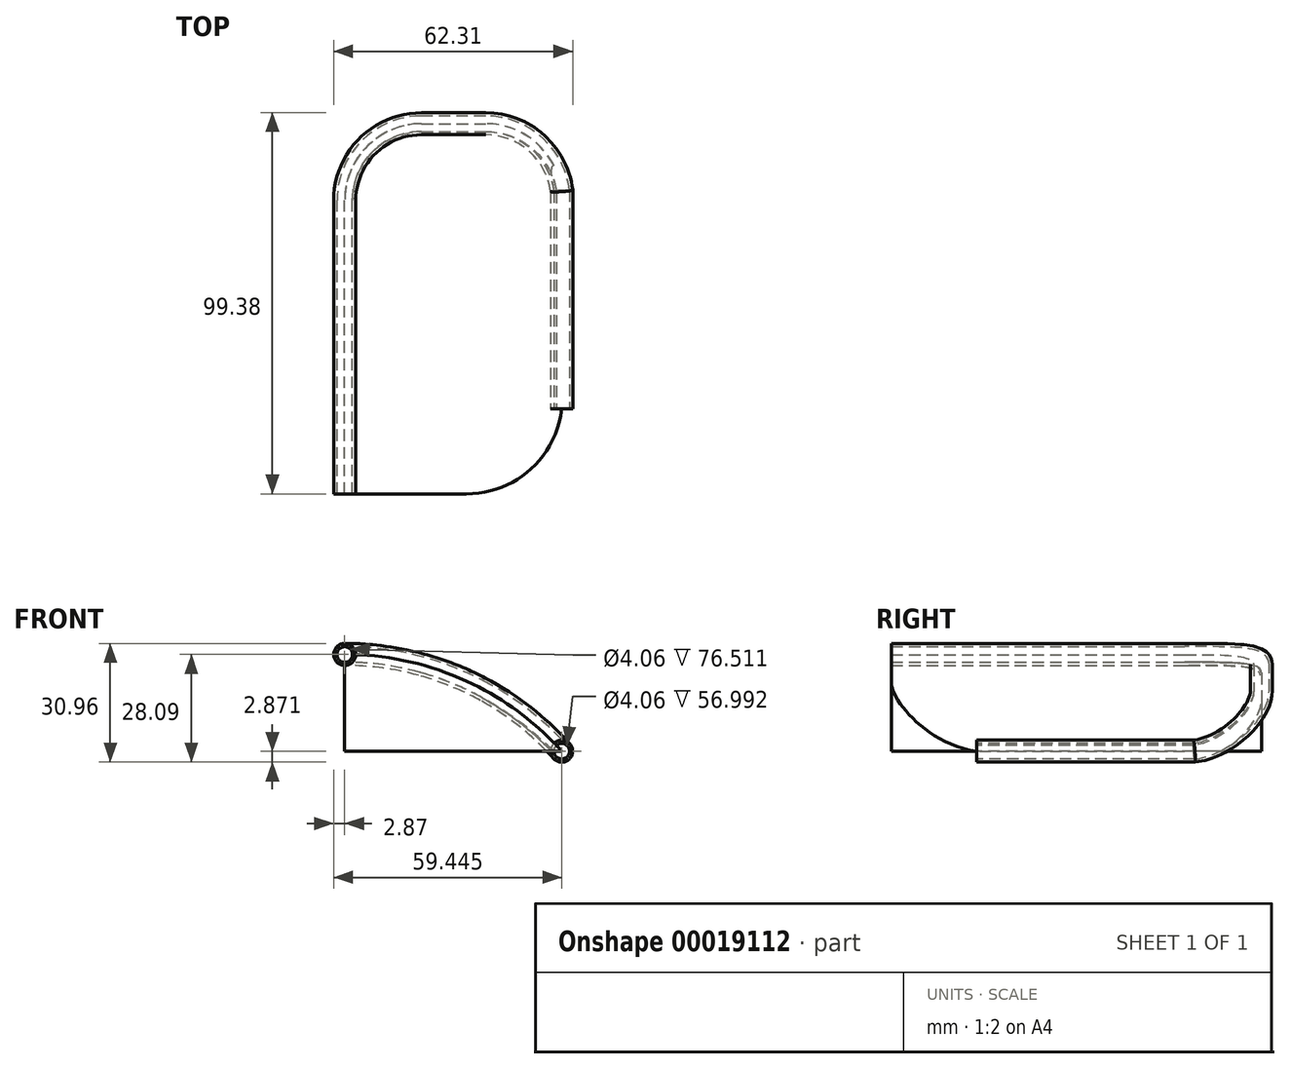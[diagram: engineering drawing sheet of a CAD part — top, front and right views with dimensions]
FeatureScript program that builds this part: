
annotation { "Feature Type Name" : "Feature", "Feature Type Description" : "" }
export const myFeature = defineFeature(function(context is Context, id is Id, definition is map)
    precondition{}
    {
        {
            var Q0;
            Q0=qCreatedBy(makeId("Front.planeOp"),FACE);
            var sketch = newSketch(context, id + "F0", { "sketchPlane" : qUnion([Q0])});
            skLineSegment(sketch, "E0.bottom", {"start": v(0, 0) * mm, "end": v(56.73, 0) * mm});
            skLineSegment(sketch, "E0.top", {"start": v(0, -44.24) * mm, "end": v(56.73, -44.24) * mm});
            skLineSegment(sketch, "E0.left", {"start": v(0, 0) * mm, "end": v(0, -44.24) * mm});
            skLineSegment(sketch, "E0.right", {"start": v(56.73, 0) * mm, "end": v(56.73, -44.24) * mm});
            skSolve(sketch);
        }
        {
            var Q0;
            Q0=makeQuery(id+"F0.imprint","IMPRINT",FACE,{"disambiguationData":[TD([[makeQuery(id+"F0.imprint","IMPRINT",EDGE,{"derivedFrom":sQuery(id+"F0.wireOp",EDGE,"E0.bottom")}),-1.0]])]});
            extrude(context, id + "F1", {"entities" : qUnion([Q0]), "depth" : 96.51 * mm});
        }
        {
            var Q0;
            Q0=makeQuery(id+"F1.opExtrude","CAP_FACE",FACE,{"disambiguationData":[OSD([sQuery(id+"F0.wireOp",EDGE,"E0.bottom"),sQuery(id+"F0.wireOp",EDGE,"E0.top"),sQuery(id+"F0.wireOp",EDGE,"E0.left"),sQuery(id+"F0.wireOp",EDGE,"E0.right")])],"isStart":false});
            var sketch = newSketch(context, id + "F2", { "sketchPlane" : qUnion([Q0])});
            skArc(sketch, "E1", {"start": v(56.73, -25.4) * mm, "mid": v(31.08, -6.64) * mm, "end": v(0, 0) * mm});
            skLineSegment(sketch, "E2", {"start": v(56.73, -25.4) * mm, "end": v(64.92, -10.77) * mm});
            skLineSegment(sketch, "E3", {"start": v(64.92, -10.77) * mm, "end": v(58.4, 12.94) * mm});
            skLineSegment(sketch, "E4", {"start": v(58.4, 12.94) * mm, "end": v(0, 7.8) * mm});
            skLineSegment(sketch, "E5", {"start": v(0, 7.8) * mm, "end": v(0, 0) * mm});
            skSolve(sketch);
        }
        {
            var Q0;
            {var subQ1=sQuery(id+"F2.wireOp",EDGE,"E1");Q0=makeQuery(id+"F2.imprint","IMPRINT",FACE,{"disambiguationData":[TD([[makeQuery(id+"F2.imprint","IMPRINT",EDGE,{"derivedFrom":subQ1}),-1.0]])]});}
            var Q1;
            {var subQ1=sQuery(id+"F2.wireOp",EDGE,"E2");Q1=makeQuery(id+"F2.imprint","IMPRINT",FACE,{"disambiguationData":[TD([[makeQuery(id+"F2.imprint","IMPRINT",EDGE,{"derivedFrom":subQ1}),1.0]])]});}
            extrude(context, id + "F3", {"entities" : qUnion([Q0, Q1]), "operationType" : NewBodyOperationType.REMOVE, "oppositeDirection" : true, "depth" : 104.35 * mm});
        }
        {
            var Q0;
            Q0=makeQuery(id+"F1.opExtrude","CAP_EDGE",EDGE,{"disambiguationData":[OSD([sQuery(id+"F0.wireOp",EDGE,"E0.right")])],"isStart":true});
            fillet(context, id + "F4", {"entities" : qUnion([Q0]), "radius" : 20 * mm, "tangentPropagation" : true, "allowEdgeOverflow" : false});
        }
        {
            var Q0;
            Q0=makeQuery(id+"F1.opExtrude","CAP_EDGE",EDGE,{"disambiguationData":[OSD([sQuery(id+"F0.wireOp",EDGE,"E0.left")])],"isStart":true});
            fillet(context, id + "F5", {"entities" : qUnion([Q0]), "radius" : 20 * mm, "tangentPropagation" : true, "allowEdgeOverflow" : false});
        }
        {
            var Q0;
            Q0=makeQuery(id+"F1.opExtrude","CAP_FACE",FACE,{"disambiguationData":[OSD([sQuery(id+"F0.wireOp",EDGE,"E0.bottom"),sQuery(id+"F0.wireOp",EDGE,"E0.top"),sQuery(id+"F0.wireOp",EDGE,"E0.left"),sQuery(id+"F0.wireOp",EDGE,"E0.right")])],"isStart":false});
            var sketch = newSketch(context, id + "F6", { "sketchPlane" : qUnion([Q0])});
            skCircle(sketch, "E6", {"center": v(0, 0) * mm, "radius": 2.87 * mm});
            skSolve(sketch);
        }
        {
            var Q0;
            Q0=makeQuery(id+"F1.opExtrude","CAP_EDGE",EDGE,{"disambiguationData":[OSD([sQuery(id+"F0.wireOp",EDGE,"E0.right")])],"isStart":false});
            fillet(context, id + "F7", {"entities" : qUnion([Q0]), "radius" : 25 * mm, "tangentPropagation" : true, "allowEdgeOverflow" : false});
        }
        {
            var Q0;
            Q0=makeQuery(id+"F1.opExtrude","SWEPT_FACE",FACE,{"disambiguationData":[OSD([sQuery(id+"F0.wireOp",EDGE,"E0.top")])]});
            extrude(context, id + "F8", {"entities" : qUnion([Q0]), "operationType" : NewBodyOperationType.REMOVE, "oppositeDirection" : true, "depth" : 19.02 * mm});
        }
        {
            var Q0;
            {var subQ1=sQuery(id+"F6.wireOp",EDGE,"E6");var subQ3=makeQuery(id+"F1.opExtrude","CAP_EDGE",EDGE,{"disambiguationData":[OSD([sQuery(id+"F0.wireOp",EDGE,"E0.left")])],"isStart":false});var subQ5=makeQuery(id+"F6.imprint","INTERSECT",VERTEX,{"derivedFrom":[subQ3,subQ1]});Q0=makeQuery(id+"F6.imprint","IMPRINT",FACE,{"disambiguationData":[TD([[makeQuery(id+"F6.imprint","IMPRINT",EDGE,{"disambiguationData":[TD([[subQ5,1.0]])],"derivedFrom":subQ1}),1.0]])]});}
            var Q1;
            {var subQ1=sQuery(id+"F6.wireOp",EDGE,"E6");var subQ3=makeQuery(id+"F1.opExtrude","CAP_EDGE",EDGE,{"disambiguationData":[OSD([sQuery(id+"F0.wireOp",EDGE,"E0.left")])],"isStart":false});var subQ5=makeQuery(id+"F6.imprint","INTERSECT",VERTEX,{"derivedFrom":[subQ3,subQ1]});Q1=makeQuery(id+"F6.imprint","IMPRINT",FACE,{"disambiguationData":[TD([[makeQuery(id+"F6.imprint","IMPRINT",EDGE,{"disambiguationData":[TD([[subQ5,-1.0]])],"derivedFrom":subQ1}),1.0]])]});}
            var Q2;
            {var subQ0=sQuery(id+"F0.wireOp",EDGE,"E0.bottom");var subQ1=sQuery(id+"F0.wireOp",EDGE,"E0.left");Q2=makeQuery(id+"F3.boolean.opBoolean","MERGE",EDGE,{"derivedFrom":[makeQuery(id+"F1.opExtrude","SWEPT_EDGE",EDGE,{"disambiguationData":[OSD([subQ0,subQ1])]}),makeQuery(id+"F3.opExtrude","SWEPT_EDGE",EDGE,{"disambiguationData":[OSD([subQ0,subQ1,sQuery(id+"F2.wireOp",EDGE,"E1"),sQuery(id+"F2.wireOp",EDGE,"E5")])]})]});}
            var Q3;
            Q3=makeQuery(id+"F5.opFillet","BLEND_EDGE",EDGE,{"blendedFrom":[makeQuery(id+"F1.opExtrude","CAP_EDGE",EDGE,{"disambiguationData":[OSD([sQuery(id+"F0.wireOp",EDGE,"E0.left")])],"isStart":true}),makeQuery(id+"F3.boolean.opBoolean","COPY",FACE,{"derivedFrom":makeQuery(id+"F3.opExtrude","SWEPT_FACE",FACE,{"disambiguationData":[OSD([sQuery(id+"F2.wireOp",EDGE,"E1")])]})})],"blendedInto":[makeQuery(id+"F3.boolean.opBoolean","COPY",FACE,{"derivedFrom":makeQuery(id+"F3.opExtrude","SWEPT_FACE",FACE,{"disambiguationData":[OSD([sQuery(id+"F2.wireOp",EDGE,"E1")])]})})]});
            var Q4;
            Q4=makeQuery(id+"F3.boolean.opBoolean","INTERSECT",EDGE,{"derivedFrom":[makeQuery(id+"F1.opExtrude","CAP_FACE",FACE,{"disambiguationData":[OSD([sQuery(id+"F0.wireOp",EDGE,"E0.bottom"),sQuery(id+"F0.wireOp",EDGE,"E0.top"),sQuery(id+"F0.wireOp",EDGE,"E0.left"),sQuery(id+"F0.wireOp",EDGE,"E0.right")])],"isStart":true}),makeQuery(id+"F3.opExtrude","SWEPT_FACE",FACE,{"disambiguationData":[OSD([sQuery(id+"F2.wireOp",EDGE,"E1")])]})]});
            var Q5;
            Q5=makeQuery(id+"F4.opFillet","BLEND_EDGE",EDGE,{"blendedFrom":[makeQuery(id+"F1.opExtrude","CAP_EDGE",EDGE,{"disambiguationData":[OSD([sQuery(id+"F0.wireOp",EDGE,"E0.right")])],"isStart":true}),makeQuery(id+"F3.boolean.opBoolean","COPY",FACE,{"derivedFrom":makeQuery(id+"F3.opExtrude","SWEPT_FACE",FACE,{"disambiguationData":[OSD([sQuery(id+"F2.wireOp",EDGE,"E1")])]})})],"blendedInto":[makeQuery(id+"F3.boolean.opBoolean","COPY",FACE,{"derivedFrom":makeQuery(id+"F3.opExtrude","SWEPT_FACE",FACE,{"disambiguationData":[OSD([sQuery(id+"F2.wireOp",EDGE,"E1")])]})})]});
            var Q6;
            Q6=makeQuery(id+"F8.boolean.opBoolean","INTERSECT",EDGE,{"derivedFrom":[makeQuery(id+"F3.boolean.opBoolean","COPY",FACE,{"derivedFrom":makeQuery(id+"F3.opExtrude","SWEPT_FACE",FACE,{"disambiguationData":[OSD([sQuery(id+"F2.wireOp",EDGE,"E1")])]})}),makeQuery(id+"F8.opExtrude","CAP_FACE",FACE,{"disambiguationData":[OSD([sQuery(id+"F0.wireOp",EDGE,"E0.top")])],"isStart":false})]});
            var Q7;
            {var subQ0=sQuery(id+"F0.wireOp",EDGE,"E0.top");var subQ1=sQuery(id+"F0.wireOp",EDGE,"E0.right");Q7=makeQuery(id+"F8.boolean.opBoolean","COPY",EDGE,{"derivedFrom":makeQuery(id+"F8.opExtrude","CAP_EDGE",EDGE,{"disambiguationData":[OSD([subQ0,subQ1]),TDD([makeQuery(id+"F7.opFillet","BLEND_EDGE",EDGE,{"blendedFrom":[makeQuery(id+"F1.opExtrude","CAP_EDGE",EDGE,{"disambiguationData":[OSD([subQ1])],"isStart":false}),makeQuery(id+"F1.opExtrude","SWEPT_FACE",FACE,{"disambiguationData":[OSD([subQ0])]})],"blendedInto":[makeQuery(id+"F1.opExtrude","SWEPT_FACE",FACE,{"disambiguationData":[OSD([subQ0])]})]})])],"isStart":false})});}
            var Q8;
            {var subQ0=sQuery(id+"F0.wireOp",EDGE,"E0.top");Q8=makeQuery(id+"F8.boolean.opBoolean","COPY",EDGE,{"derivedFrom":makeQuery(id+"F8.opExtrude","CAP_EDGE",EDGE,{"disambiguationData":[OSD([subQ0]),TDD([makeQuery(id+"F1.opExtrude","CAP_EDGE",EDGE,{"disambiguationData":[OSD([subQ0])],"isStart":false})])],"isStart":false})});}
            sweep(context, id + "F9", {"profiles" : qUnion([Q0, Q1]), "path" : qUnion([Q2, Q3, Q4, Q5, Q6, Q7, Q8])});
        }
        {
            var Q0;
            Q0=makeQuery(id+"F9.opSweep","CAP_FACE",FACE,{"disambiguationData":[OSD([sQuery(id+"F0.wireOp",EDGE,"E0.bottom"),sQuery(id+"F0.wireOp",EDGE,"E0.left"),sQuery(id+"F2.wireOp",EDGE,"E1"),sQuery(id+"F2.wireOp",EDGE,"E5"),sQuery(id+"F6.wireOp",EDGE,"E6")])],"isStart":true});
            var sketch = newSketch(context, id + "F10", { "sketchPlane" : qUnion([Q0])});
            skCircle(sketch, "E7", {"center": v(0, 0) * mm, "radius": 2.03 * mm});
            skSolve(sketch);
        }
        {
            var Q0;
            Q0=makeQuery(id+"F10.imprint","IMPRINT",FACE,{"disambiguationData":[TD([[makeQuery(id+"F10.imprint","IMPRINT",EDGE,{"derivedFrom":sQuery(id+"F10.wireOp",EDGE,"E7")}),1.0]])]});
            var Q1;
            {var subQ0=sQuery(id+"F0.wireOp",EDGE,"E0.bottom");var subQ1=sQuery(id+"F0.wireOp",EDGE,"E0.left");Q1=makeQuery(id+"F3.boolean.opBoolean","MERGE",EDGE,{"derivedFrom":[makeQuery(id+"F1.opExtrude","SWEPT_EDGE",EDGE,{"disambiguationData":[OSD([subQ0,subQ1])]}),makeQuery(id+"F3.opExtrude","SWEPT_EDGE",EDGE,{"disambiguationData":[OSD([subQ0,subQ1,sQuery(id+"F2.wireOp",EDGE,"E1"),sQuery(id+"F2.wireOp",EDGE,"E5")])]})]});}
            var Q2;
            Q2=makeQuery(id+"F5.opFillet","BLEND_EDGE",EDGE,{"blendedFrom":[makeQuery(id+"F1.opExtrude","CAP_EDGE",EDGE,{"disambiguationData":[OSD([sQuery(id+"F0.wireOp",EDGE,"E0.left")])],"isStart":true}),makeQuery(id+"F3.boolean.opBoolean","COPY",FACE,{"derivedFrom":makeQuery(id+"F3.opExtrude","SWEPT_FACE",FACE,{"disambiguationData":[OSD([sQuery(id+"F2.wireOp",EDGE,"E1")])]})})],"blendedInto":[makeQuery(id+"F3.boolean.opBoolean","COPY",FACE,{"derivedFrom":makeQuery(id+"F3.opExtrude","SWEPT_FACE",FACE,{"disambiguationData":[OSD([sQuery(id+"F2.wireOp",EDGE,"E1")])]})})]});
            var Q3;
            Q3=makeQuery(id+"F3.boolean.opBoolean","INTERSECT",EDGE,{"derivedFrom":[makeQuery(id+"F1.opExtrude","CAP_FACE",FACE,{"disambiguationData":[OSD([sQuery(id+"F0.wireOp",EDGE,"E0.bottom"),sQuery(id+"F0.wireOp",EDGE,"E0.top"),sQuery(id+"F0.wireOp",EDGE,"E0.left"),sQuery(id+"F0.wireOp",EDGE,"E0.right")])],"isStart":true}),makeQuery(id+"F3.opExtrude","SWEPT_FACE",FACE,{"disambiguationData":[OSD([sQuery(id+"F2.wireOp",EDGE,"E1")])]})]});
            var Q4;
            Q4=makeQuery(id+"F4.opFillet","BLEND_EDGE",EDGE,{"blendedFrom":[makeQuery(id+"F1.opExtrude","CAP_EDGE",EDGE,{"disambiguationData":[OSD([sQuery(id+"F0.wireOp",EDGE,"E0.right")])],"isStart":true}),makeQuery(id+"F3.boolean.opBoolean","COPY",FACE,{"derivedFrom":makeQuery(id+"F3.opExtrude","SWEPT_FACE",FACE,{"disambiguationData":[OSD([sQuery(id+"F2.wireOp",EDGE,"E1")])]})})],"blendedInto":[makeQuery(id+"F3.boolean.opBoolean","COPY",FACE,{"derivedFrom":makeQuery(id+"F3.opExtrude","SWEPT_FACE",FACE,{"disambiguationData":[OSD([sQuery(id+"F2.wireOp",EDGE,"E1")])]})})]});
            var Q5;
            Q5=makeQuery(id+"F8.boolean.opBoolean","INTERSECT",EDGE,{"derivedFrom":[makeQuery(id+"F3.boolean.opBoolean","COPY",FACE,{"derivedFrom":makeQuery(id+"F3.opExtrude","SWEPT_FACE",FACE,{"disambiguationData":[OSD([sQuery(id+"F2.wireOp",EDGE,"E1")])]})}),makeQuery(id+"F8.opExtrude","CAP_FACE",FACE,{"disambiguationData":[OSD([sQuery(id+"F0.wireOp",EDGE,"E0.top")])],"isStart":false})]});
            var Q6;
            {var subQ0=sQuery(id+"F0.wireOp",EDGE,"E0.top");var subQ1=sQuery(id+"F0.wireOp",EDGE,"E0.right");Q6=makeQuery(id+"F8.boolean.opBoolean","COPY",EDGE,{"derivedFrom":makeQuery(id+"F8.opExtrude","CAP_EDGE",EDGE,{"disambiguationData":[OSD([subQ0,subQ1]),TDD([makeQuery(id+"F7.opFillet","BLEND_EDGE",EDGE,{"blendedFrom":[makeQuery(id+"F1.opExtrude","CAP_EDGE",EDGE,{"disambiguationData":[OSD([subQ1])],"isStart":false}),makeQuery(id+"F1.opExtrude","SWEPT_FACE",FACE,{"disambiguationData":[OSD([subQ0])]})],"blendedInto":[makeQuery(id+"F1.opExtrude","SWEPT_FACE",FACE,{"disambiguationData":[OSD([subQ0])]})]})])],"isStart":false})});}
            var Q7;
            {var subQ0=sQuery(id+"F0.wireOp",EDGE,"E0.top");Q7=makeQuery(id+"F8.boolean.opBoolean","COPY",EDGE,{"derivedFrom":makeQuery(id+"F8.opExtrude","CAP_EDGE",EDGE,{"disambiguationData":[OSD([subQ0]),TDD([makeQuery(id+"F1.opExtrude","CAP_EDGE",EDGE,{"disambiguationData":[OSD([subQ0])],"isStart":false})])],"isStart":false})});}
            sweep(context, id + "F11", {"operationType" : NewBodyOperationType.REMOVE, "profiles" : qUnion([Q0]), "path" : qUnion([Q1, Q2, Q3, Q4, Q5, Q6, Q7])});
        }
    });
